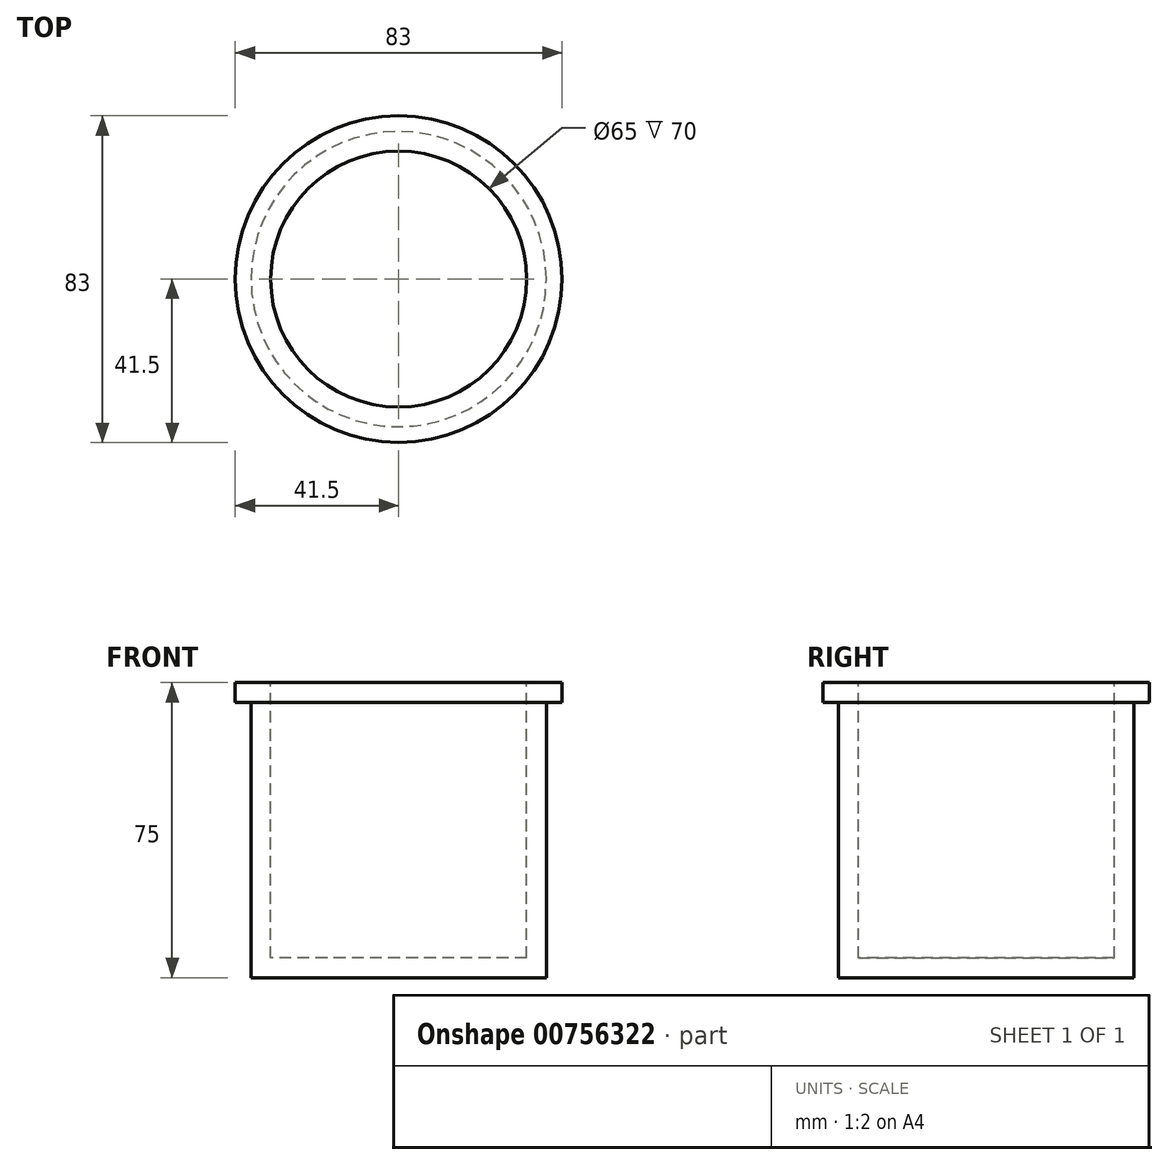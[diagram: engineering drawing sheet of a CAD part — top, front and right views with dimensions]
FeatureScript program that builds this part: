
annotation { "Feature Type Name" : "Feature", "Feature Type Description" : "" }
export const myFeature = defineFeature(function(context is Context, id is Id, definition is map)
    precondition{}
    {
        {
            var Q0;
            Q0=qCreatedBy(makeId("Top.planeOp"),FACE);
            var sketch = newSketch(context, id + "F0", { "sketchPlane" : qUnion([Q0])});
            skCircle(sketch, "E0", {"center": v(0, 0) * mm, "radius": 41.5 * mm});
            skSolve(sketch);
        }
        {
            var Q0;
            Q0 = qSketchRegion(id + "F0", true);
            extrude(context, id + "F1", {"entities" : qUnion([Q0]), "depth" : 75 * mm, "offsetDistance" : 25 * mm});
        }
        {
            var Q0;
            Q0=makeQuery(id+"F1.opExtrude","CAP_FACE",FACE,{"disambiguationData":[OSD([sQuery(id+"F0.wireOp",EDGE,"E0")])],"isStart":false});
            var sketch = newSketch(context, id + "F2", { "sketchPlane" : qUnion([Q0])});
            skCircle(sketch, "E1", {"center": v(0, 0) * mm, "radius": 32.5 * mm});
            skSolve(sketch);
        }
        {
            var Q0;
            Q0=makeQuery(id+"F2.imprint","IMPRINT",FACE,{"disambiguationData":[TD([[makeQuery(id+"F2.imprint","IMPRINT",EDGE,{"derivedFrom":sQuery(id+"F2.wireOp",EDGE,"E1")}),1.0]])]});
            extrude(context, id + "F3", {"entities" : qUnion([Q0]), "operationType" : NewBodyOperationType.REMOVE, "oppositeDirection" : true, "depth" : 70 * mm, "offsetDistance" : 25 * mm});
        }
        {
            var Q0;
            Q0=makeQuery(id+"F1.opExtrude","CAP_FACE",FACE,{"disambiguationData":[OSD([sQuery(id+"F0.wireOp",EDGE,"E0")])],"isStart":true});
            var sketch = newSketch(context, id + "F4", { "sketchPlane" : qUnion([Q0])});
            skCircle(sketch, "E2", {"center": v(0, 0) * mm, "radius": 37.5 * mm});
            skSolve(sketch);
        }
        {
            var Q0;
            Q0=makeQuery(id+"F4.imprint","IMPRINT",FACE,{"disambiguationData":[TD([[makeQuery(id+"F4.imprint","IMPRINT",EDGE,{"derivedFrom":sQuery(id+"F4.wireOp",EDGE,"E2")}),-1.0]])]});
            extrude(context, id + "F5", {"entities" : qUnion([Q0]), "operationType" : NewBodyOperationType.REMOVE, "oppositeDirection" : true, "depth" : 70 * mm, "offsetDistance" : 25 * mm});
        }
    });
